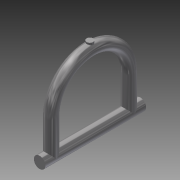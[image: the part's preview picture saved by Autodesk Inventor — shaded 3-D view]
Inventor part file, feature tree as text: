
AUTODESK INVENTOR PART (.ipt)
format: ipt  version: 2014 (Build 180170000, 170)  size: 179,712 bytes
history: native  units: in
note: dims shown in document units (in); Inventor stores cm internally (conversion verified against a paired STEP export)
features: sketch x5, extrude x3, plane x2, revolve x1
ambient origin geometry x8: Origin, YZ Plane, XZ Plane, XY Plane, X Axis, Y Axis, Z Axis, Center Point
bodies: Solid1 (feature_tree)
feature tree (11):
  extrude  "Extrusion1"  Depth=1.75in TaperAngle=0.0deg
  sketch  "Sketch2"  dims[d4=0.2in d6=0.2in]
  plane  "Work Plane1"
  extrude  "Extrusion2"  Depth=0.2in
  revolve  "Revolution1"  [1 undecoded]
  plane  "Work Plane3"
  extrude  "Extrusion3"  Depth=0.1in
  sketch  "Sketch1"  dims[d0=0.2in d2=1.75in d3=0.0in]
  sketch  "Sketch3"  dims[d7=0.2in d8=0.2in]
  sketch  "Sketch4"  dims[d9=0.5in d10=0.1in d11=0.0in d12=0.0in d14=1.35in]
  sketch  "Sketch6"  dims[d15=180.0deg d16=1.2in d17=0.1in d18=0.0in]
note: 1 required parameter value undecoded (feature->parameter linkage not recoverable at this tier; creation-order binding heuristic only, values carry confidence <= 0.55)
